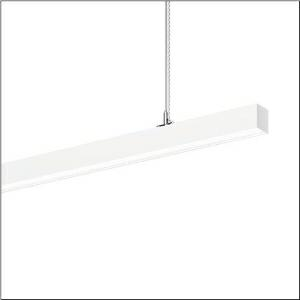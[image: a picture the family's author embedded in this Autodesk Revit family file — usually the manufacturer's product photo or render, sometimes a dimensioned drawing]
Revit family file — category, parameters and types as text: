
# Revit family: silica_r__21_51mx33tbt9w_4d61
name_source: partatom
category: Lighting Fixtures
units: mm (PartAtom-declared; Revit-internal decimal feet)

## family parameters
Cut with Voids When Loaded = No
Host = Face
Light Source = No
Part Type = Normal
Room Calculation Point = No
Round Connector Dimension = Use Diameter
Shared = No

## types (1)
- --- (1 x LED, 7170 lm, 67.4 W, 6500K)
    Apparent Load = 67 VA
    CIE Flux Codes = 78 96 99 56 100
    Color Rendering = 80
    Color Temperature = 6500K
    Default Elevation = 1800 mm
    Description = Silica® 21, office luminaire, primary optical cover: prismatic diffuser, of PMMA, CAT 2 (L<= 3000cd/m²), light emission: direct/indirect distribution, primary light characteristic: symmetric, installation type: suspended mounting, LED, rated luminous flux: 7.170lm, luminous efficacy: 101lm/W, light colour: 8tw, colour temperature: 2700..6500K, control gear: DALI DT8, with terminal, 3+2-pole, max. 2.5mm², mains connection: 220..240V, AC, 50/60Hz, rated input power: 70.8W, luminaire housing, of aluminium, traffic white (RAL 9016), length: 1.504mm, width: 53mm, height: 53mm, protection rating (complete): IP20, insulation class (complete): insulation class I (protective earthing), certification: CE, permissible operating ambient temperature: 0..+35°C, standard: EN 50419, packaging unit: 1 piece
    Height = 53 mm
    Lamp = 1 x LED
    Lamp Light Flux = 7170 lm
    Lamp Power = 67.4 W
    Lamp count = 1
    Length = 1504 mm
    Luminous efficacy = 106 lm/W
    Manufacturer = Siteco
    ModVariant = No
    Model = 51MX33TBT9W
    Mounting Place = Ceiling
    Mounting Type = Pendant
    Number of Poles = 1
    OnlyDefault = Yes
    Power Factor = 1
    Product Name = Silica® 21
    Product group = office luminaire | ceiling pendant
    ProductGroupID = 904
    Protection Class = Protection class I
    Protection Degree = IP 20
    RLX_Detail_Level = 1
    RLX_Emergency_Light_Flux = 0 lm
    RLX_Emergency_Type = 0
    RLX_Emergency_Type_DB = No
    RlxData = <blob elided: 18189 chars, md5=96198203>
    Socket = socket
    Standby Power = 0 W
    System Light Flux = 7170 lm
    System Power = 67 W
    Type Comments = individual setting
    Type Image = l_1349007.jpg
    URL = http://relux.com
    VarID = @adj_139776
    Voltage = 0 V
    Weight = 0.00 kg
    Width = 53 mm

## geometry (parser evidence)
native form markers: Blend x4, Sweep x13
no freeform markers — native parametric forms only
